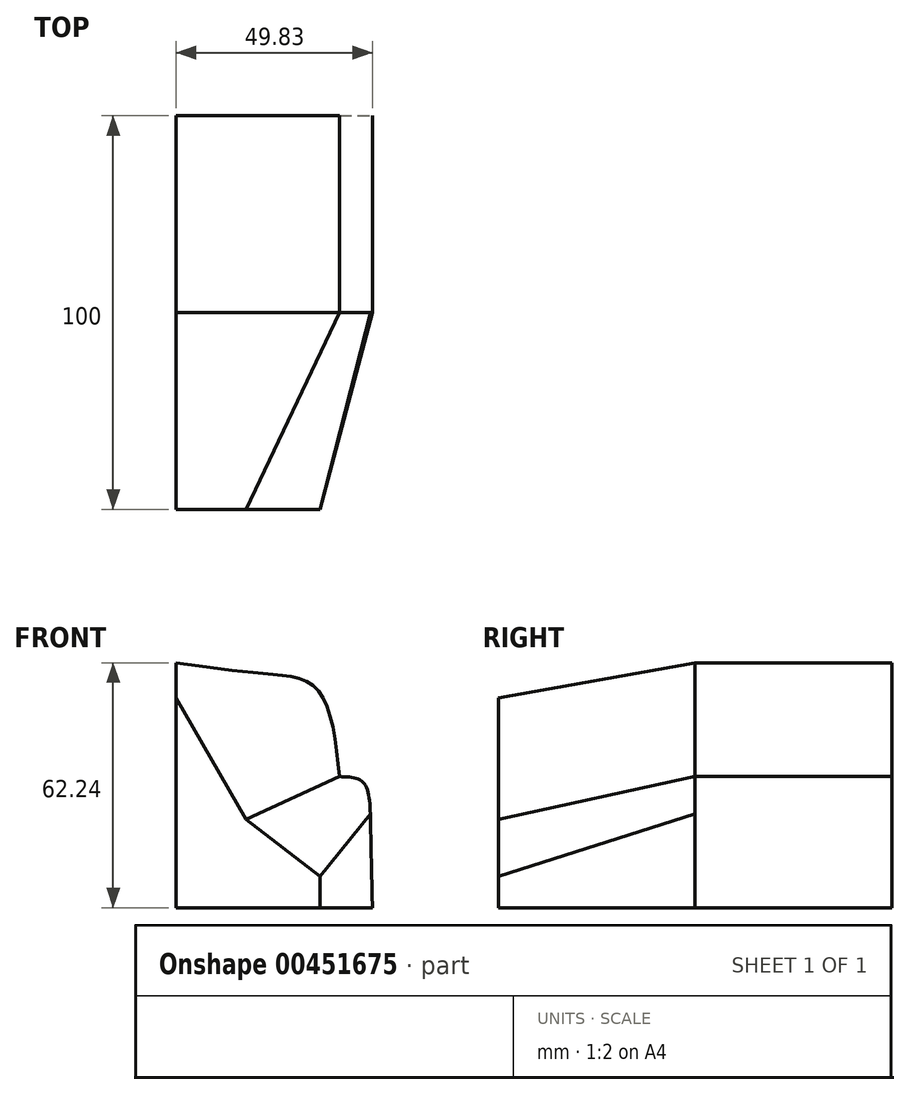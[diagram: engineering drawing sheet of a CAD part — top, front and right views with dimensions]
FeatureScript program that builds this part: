
annotation { "Feature Type Name" : "Feature", "Feature Type Description" : "" }
export const myFeature = defineFeature(function(context is Context, id is Id, definition is map)
    precondition{}
    {
        {
            var Q0;
            Q0=qCreatedBy(makeId("Front.planeOp"),FACE);
            cPlane(context, id + "F0", {"entities" : qUnion([Q0]), "cplaneType" : CPlaneType.OFFSET, "offset" : 50 * mm, "width" : 150 * mm, "height" : 150 * mm});
        }
        {
            var Q0;
            Q0=qCreatedBy(id+"F0.planeOp",FACE);
            var sketch = newSketch(context, id + "F1", { "sketchPlane" : qUnion([Q0])});
            skLineSegment(sketch, "E0", {"start": v(-25, -26) * mm, "end": v(-25, 36.25) * mm});
            skFitSpline(sketch, "E1", {"points": [v(-25, 36.25) * mm, v(-2.05, 33.42) * mm, v(10.68, 29.65) * mm, v(16.5, 7.33) * mm], "startDerivative": vector(66.37, -9.11) * mm, "endDerivative": vector(8.12, -75.5) * mm});
            skFitSpline(sketch, "E2", {"points": [v(16.5, 7.33) * mm, v(22.47, 5.91) * mm, v(24.36, -4.15) * mm, v(24.83, -26) * mm], "startDerivative": vector(29.08, -0.49) * mm, "endDerivative": vector(1.12, -51) * mm});
            skLineSegment(sketch, "E3", {"start": v(24.83, -26) * mm, "end": v(-25, -26) * mm});
            skSolve(sketch);
        }
        {
            var Q0;
            Q0=qCreatedBy(id+"F0.planeOp",FACE);
            cPlane(context, id + "F2", {"entities" : qUnion([Q0]), "cplaneType" : CPlaneType.OFFSET, "offset" : 50 * mm, "width" : 150 * mm, "height" : 150 * mm});
        }
        {
            var Q0;
            Q0=qCreatedBy(id+"F2.planeOp",FACE);
            var sketch = newSketch(context, id + "F3", { "sketchPlane" : qUnion([Q0])});
            skLineSegment(sketch, "E4", {"start": v(-25, -26) * mm, "end": v(-25, 36.25) * mm});
            skFitSpline(sketch, "E5", {"points": [v(-25, 36.25) * mm, v(-2.05, 33.42) * mm, v(10.68, 29.65) * mm, v(16.5, 7.33) * mm], "startDerivative": vector(66.37, -9.11) * mm, "endDerivative": vector(8.12, -75.5) * mm});
            skFitSpline(sketch, "E6", {"points": [v(16.5, 7.33) * mm, v(22.47, 5.91) * mm, v(24.36, -4.15) * mm, v(24.83, -26) * mm], "startDerivative": vector(29.08, -0.49) * mm, "endDerivative": vector(1.12, -51) * mm});
            skLineSegment(sketch, "E7", {"start": v(24.83, -26) * mm, "end": v(-25, -26) * mm});
            skSolve(sketch);
        }
        {
            var Q0;
            Q0=qCreatedBy(id+"F2.planeOp",FACE);
            cPlane(context, id + "F4", {"entities" : qUnion([Q0]), "cplaneType" : CPlaneType.OFFSET, "offset" : 50 * mm, "width" : 150 * mm, "height" : 150 * mm});
        }
        {
            var Q0;
            Q0=qCreatedBy(id+"F4.planeOp",FACE);
            var sketch = newSketch(context, id + "F5", { "sketchPlane" : qUnion([Q0])});
            skLineSegment(sketch, "E8", {"start": v(-25, -26) * mm, "end": v(-25, 27.3) * mm});
            skLineSegment(sketch, "E9", {"start": v(-25, 27.3) * mm, "end": v(-7.24, -3.52) * mm});
            skLineSegment(sketch, "E10", {"start": v(-7.24, -3.52) * mm, "end": v(11.47, -17.98) * mm});
            skLineSegment(sketch, "E11", {"start": v(11.47, -17.98) * mm, "end": v(11.47, -26) * mm});
            skLineSegment(sketch, "E12", {"start": v(-25, -26) * mm, "end": v(11.47, -26) * mm});
            skSolve(sketch);
        }
        {
            var Q0;
            Q0=makeQuery(id+"F1.imprint","IMPRINT",FACE,{"disambiguationData":[TD([[makeQuery(id+"F1.imprint","IMPRINT",EDGE,{"derivedFrom":sQuery(id+"F1.wireOp",EDGE,"E0")}),-1.0]])]});
            var Q1;
            Q1=makeQuery(id+"F3.imprint","IMPRINT",FACE,{"disambiguationData":[TD([[makeQuery(id+"F3.imprint","IMPRINT",EDGE,{"derivedFrom":sQuery(id+"F3.wireOp",EDGE,"E4")}),-1.0]])]});
            loft(context, id + "F6", {"sheetProfilesArray" : [{ "sheetProfileEntities" : qUnion([Q0]) }, { "sheetProfileEntities" : qUnion([Q1]) }]});
        }
        {
            var Q1;
            Q1=makeQuery(id+"F6.opLoft","CAP_FACE",FACE,{"disambiguationData":[OSD([makeQuery(id+"F3.imprint","IMPRINT",FACE,{"disambiguationData":[TD([[makeQuery(id+"F3.imprint","IMPRINT",EDGE,{"derivedFrom":sQuery(id+"F3.wireOp",EDGE,"E4")}),-1.0]])]})])],"isStart":true});
            var Q2;
            Q2=makeQuery(id+"F5.imprint","IMPRINT",FACE,{"disambiguationData":[TD([[makeQuery(id+"F5.imprint","IMPRINT",EDGE,{"derivedFrom":sQuery(id+"F5.wireOp",EDGE,"E8")}),-1.0]])]});
            var Q3;
            Q3=sQuery(id+"F5.wireOp",VERTEX,"E12.end");
            var Q4;
            Q4=makeQuery(id+"F6.opLoft","MID_CAP_VERTEX",VERTEX,{"disambiguationData":[OSD([sQuery(id+"F3.wireOp",EDGE,"E6"),sQuery(id+"F3.wireOp",EDGE,"E7")])],"capPos":1.0});
            loft(context, id + "F7", {"operationType" : NewBodyOperationType.ADD, "sheetProfilesArray" : [{ "sheetProfileEntities" : qUnion([Q1]) }, { "sheetProfileEntities" : qUnion([Q2]) }], "matchConnections" : true, "connections" : [{ "connectionEntities" : qUnion([Q3, Q4]), "connectionEdgeQueries" : qUnion([]), "connectionEdgeParameters" : [] }]});
        }
    });
